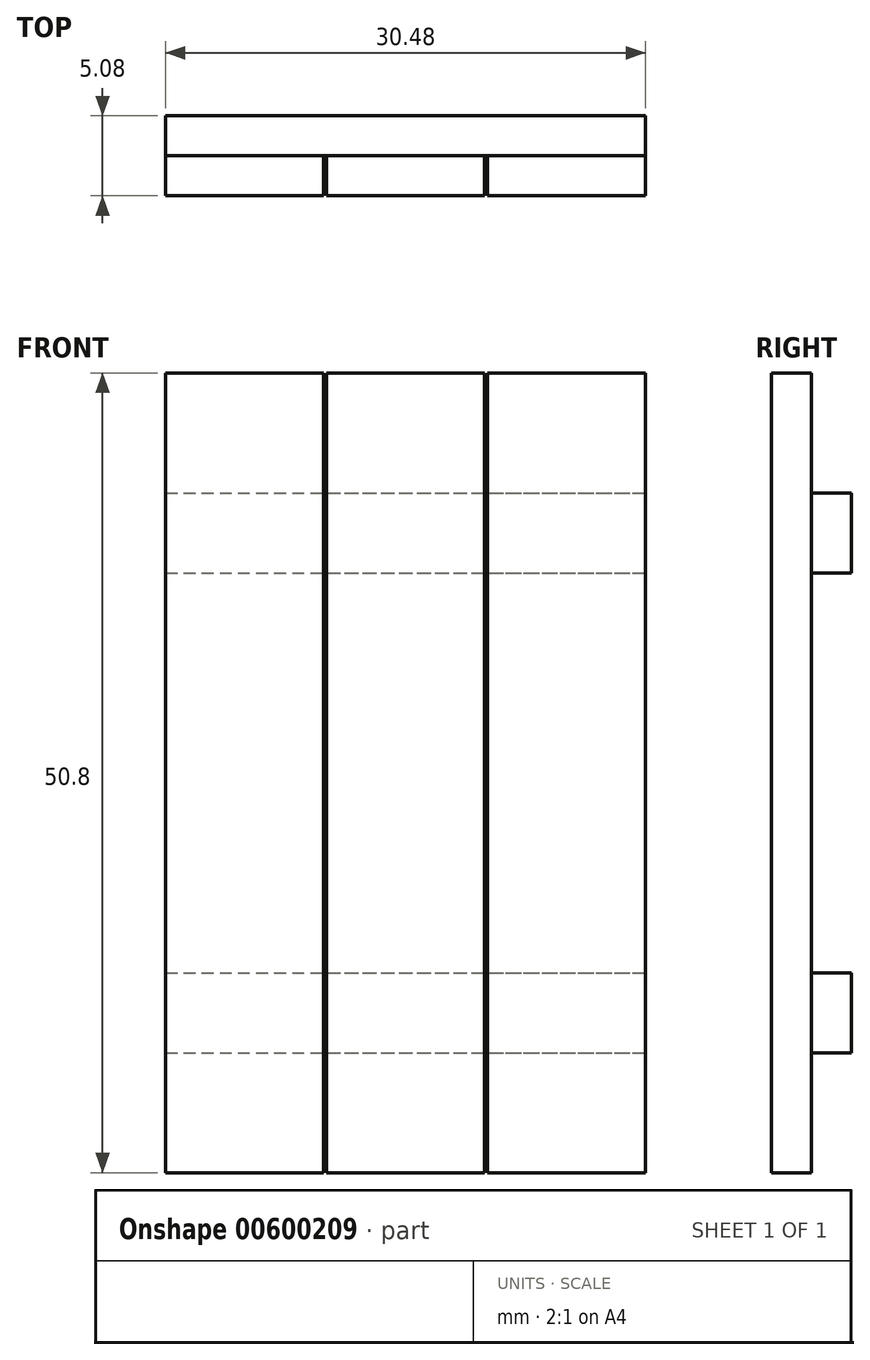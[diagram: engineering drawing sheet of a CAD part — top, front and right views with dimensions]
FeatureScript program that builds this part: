
annotation { "Feature Type Name" : "Feature", "Feature Type Description" : "" }
export const myFeature = defineFeature(function(context is Context, id is Id, definition is map)
    precondition{}
    {
        {
            var Q0;
            Q0=qCreatedBy(makeId("Front.planeOp"),FACE);
            var sketch = newSketch(context, id + "F0", { "sketchPlane" : qUnion([Q0])});
            skLineSegment(sketch, "E0.bottom", {"start": v(0, 0) * mm, "end": v(10.03, 0) * mm});
            skLineSegment(sketch, "E0.top", {"start": v(0, 50.8) * mm, "end": v(10.03, 50.8) * mm});
            skLineSegment(sketch, "E0.left", {"start": v(0, 0) * mm, "end": v(0, 50.8) * mm});
            skLineSegment(sketch, "E0.right", {"start": v(10.03, 0) * mm, "end": v(10.03, 50.8) * mm});
            skLineSegment(sketch, "E1.bottom", {"start": v(20.45, 0) * mm, "end": v(30.48, 0) * mm});
            skLineSegment(sketch, "E1.top", {"start": v(20.45, 50.8) * mm, "end": v(30.48, 50.8) * mm});
            skLineSegment(sketch, "E1.left", {"start": v(20.45, 0) * mm, "end": v(20.45, 50.8) * mm});
            skLineSegment(sketch, "E1.right", {"start": v(30.48, 0) * mm, "end": v(30.48, 50.8) * mm});
            skLineSegment(sketch, "E2.bottom", {"start": v(10.22, 0) * mm, "end": v(20.26, 0) * mm});
            skLineSegment(sketch, "E2.top", {"start": v(10.22, 50.8) * mm, "end": v(20.26, 50.8) * mm});
            skLineSegment(sketch, "E2.left", {"start": v(10.22, 0) * mm, "end": v(10.22, 50.8) * mm});
            skLineSegment(sketch, "E2.right", {"start": v(20.26, 0) * mm, "end": v(20.26, 50.8) * mm});
            skSolve(sketch);
        }
        {
            var Q0;
            Q0=makeQuery(id+"F0.imprint","IMPRINT",FACE,{"disambiguationData":[TD([[makeQuery(id+"F0.imprint","IMPRINT",EDGE,{"derivedFrom":sQuery(id+"F0.wireOp",EDGE,"E0.bottom")}),1.0]])]});
            var Q1;
            Q1=makeQuery(id+"F0.imprint","IMPRINT",FACE,{"disambiguationData":[TD([[makeQuery(id+"F0.imprint","IMPRINT",EDGE,{"derivedFrom":sQuery(id+"F0.wireOp",EDGE,"E1.bottom")}),1.0]])]});
            var Q2;
            Q2=makeQuery(id+"F0.imprint","IMPRINT",FACE,{"disambiguationData":[TD([[makeQuery(id+"F0.imprint","IMPRINT",EDGE,{"derivedFrom":sQuery(id+"F0.wireOp",EDGE,"E2.bottom")}),1.0]])]});
            extrude(context, id + "F1", {"entities" : qUnion([Q0, Q1, Q2]), "depth" : 2.54 * mm, "offsetDistance" : 25.4 * mm});
        }
        {
            var Q0;
            Q0=qCreatedBy(makeId("Front.planeOp"),FACE);
            var sketch = newSketch(context, id + "F2", { "sketchPlane" : qUnion([Q0])});
            skLineSegment(sketch, "E3.bottom", {"start": v(0, 7.62) * mm, "end": v(30.48, 7.62) * mm});
            skLineSegment(sketch, "E3.top", {"start": v(0, 12.7) * mm, "end": v(30.48, 12.7) * mm});
            skLineSegment(sketch, "E3.left", {"start": v(0, 7.62) * mm, "end": v(0, 12.7) * mm});
            skLineSegment(sketch, "E3.right", {"start": v(30.48, 7.62) * mm, "end": v(30.48, 12.7) * mm});
            skLineSegment(sketch, "E4.bottom", {"start": v(0, 38.1) * mm, "end": v(30.48, 38.1) * mm});
            skLineSegment(sketch, "E4.top", {"start": v(0, 43.18) * mm, "end": v(30.48, 43.18) * mm});
            skLineSegment(sketch, "E4.left", {"start": v(0, 38.1) * mm, "end": v(0, 43.18) * mm});
            skLineSegment(sketch, "E4.right", {"start": v(30.48, 38.1) * mm, "end": v(30.48, 43.18) * mm});
            skSolve(sketch);
        }
        {
            var Q0;
            Q0=makeQuery(id+"F2.imprint","IMPRINT",FACE,{"disambiguationData":[TD([[makeQuery(id+"F2.imprint","IMPRINT",EDGE,{"derivedFrom":sQuery(id+"F2.wireOp",EDGE,"E4.bottom")}),1.0]])]});
            var Q1;
            Q1=makeQuery(id+"F2.imprint","IMPRINT",FACE,{"disambiguationData":[TD([[makeQuery(id+"F2.imprint","IMPRINT",EDGE,{"derivedFrom":sQuery(id+"F2.wireOp",EDGE,"E3.bottom")}),1.0]])]});
            extrude(context, id + "F3", {"entities" : qUnion([Q0, Q1]), "oppositeDirection" : true, "depth" : 2.54 * mm, "offsetDistance" : 25.4 * mm});
        }
    });
